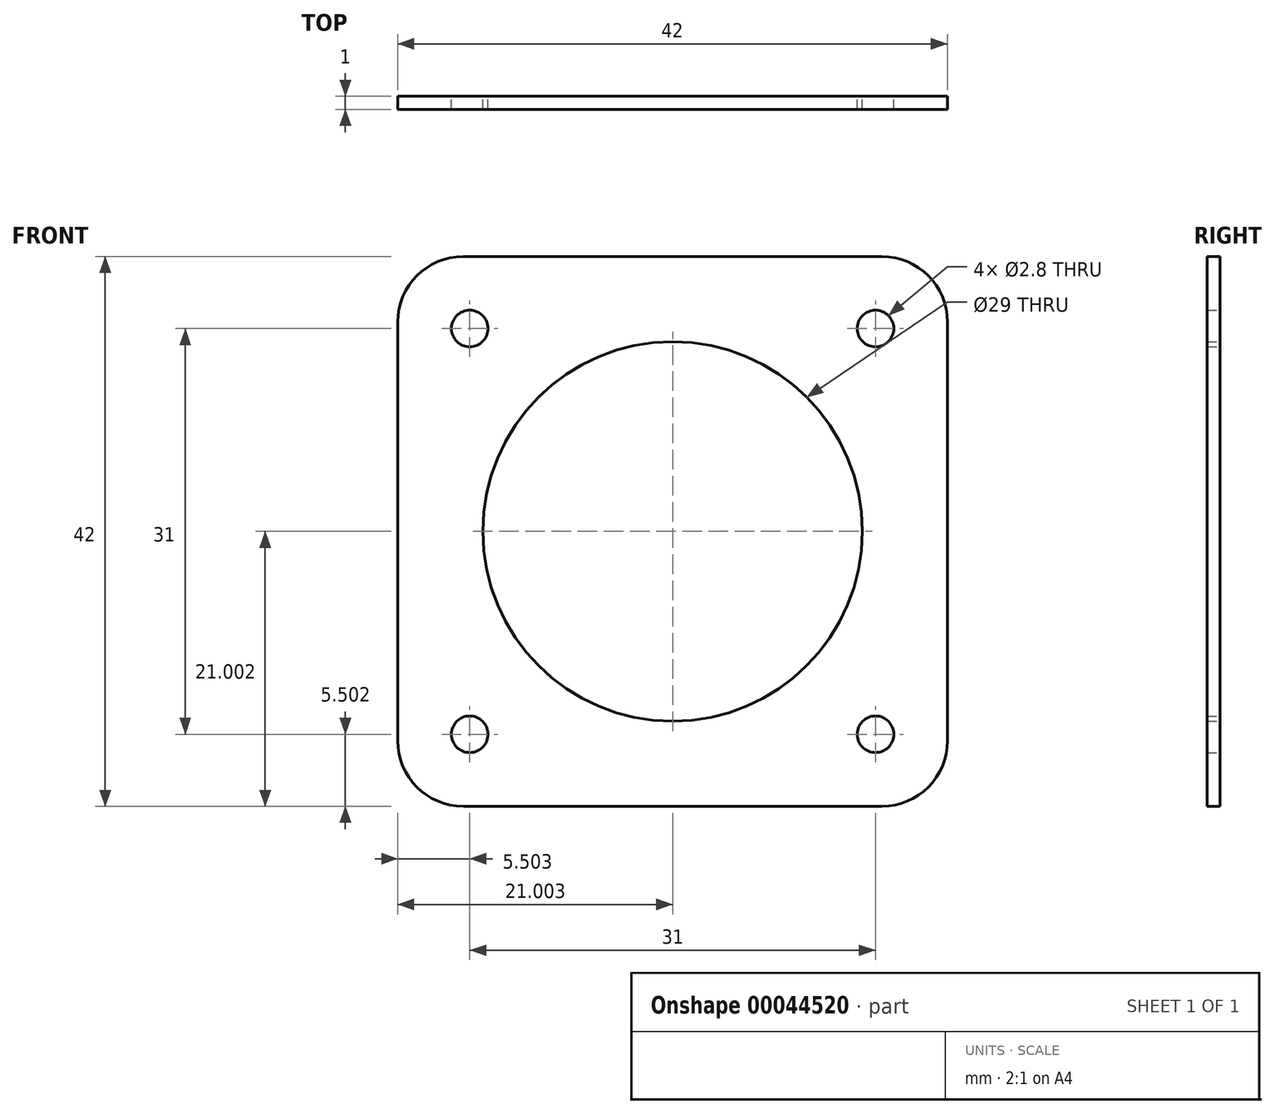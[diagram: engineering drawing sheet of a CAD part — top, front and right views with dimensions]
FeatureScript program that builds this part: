
annotation { "Feature Type Name" : "Feature", "Feature Type Description" : "" }
export const myFeature = defineFeature(function(context is Context, id is Id, definition is map)
    precondition{}
    {
        {
            var Q0;
            Q0=qCreatedBy(makeId("Front.planeOp"),FACE);
            var sketch = newSketch(context, id + "F0", { "sketchPlane" : qUnion([Q0])});
            skPoint(sketch, "E0", {"position": v(2.9, 11.96) * mm});
            skPoint(sketch, "E1", {"position": v(-28.1, 11.96) * mm});
            skPoint(sketch, "E2", {"position": v(-28.1, -19.04) * mm});
            skPoint(sketch, "E3", {"position": v(2.9, -19.04) * mm});
            skLineSegment(sketch, "E4.bottom", {"start": v(-33.6, 17.46) * mm, "end": v(8.4, 17.46) * mm});
            skLineSegment(sketch, "E4.top", {"start": v(-33.6, -24.54) * mm, "end": v(8.4, -24.54) * mm});
            skLineSegment(sketch, "E4.left", {"start": v(-33.6, 17.46) * mm, "end": v(-33.6, -24.54) * mm});
            skLineSegment(sketch, "E4.right", {"start": v(8.4, 17.46) * mm, "end": v(8.4, -24.54) * mm});
            skPoint(sketch, "E5", {"position": v(-12.6, -3.54) * mm});
            skSolve(sketch);
        }
        {
            var Q0;
            Q0=makeQuery(id+"F0.imprint","IMPRINT",FACE,{"disambiguationData":[TD([[makeQuery(id+"F0.imprint","IMPRINT",EDGE,{"derivedFrom":sQuery(id+"F0.wireOp",EDGE,"E4.bottom")}),-1.0]])]});
            extrude(context, id + "F1", {"entities" : qUnion([Q0]), "depth" : 1 * mm});
        }
        {
            var Q0;
            Q0=sQuery(id+"F0.wireOp",VERTEX,"E5");
            var Q1;
            Q1=makeQuery(id+"F1.opExtrude","SWEPT_BODY",BODY,{"disambiguationData":[OSD([sQuery(id+"F0.wireOp",EDGE,"E4.bottom"),sQuery(id+"F0.wireOp",EDGE,"E4.top"),sQuery(id+"F0.wireOp",EDGE,"E4.left"),sQuery(id+"F0.wireOp",EDGE,"E4.right")])]});
            hole(context, id + "F2", {"style" : HoleStyle.SIMPLE, "holeDiameter" : 29 * mm, "endStyle" : HoleEndStyle.THROUGH, "oppositeDirection" : true, "locations" : qUnion([Q0]), "scope" : qUnion([Q1])});
        }
        {
            var Q0;
            Q0=sQuery(id+"F0.wireOp",VERTEX,"E1");
            var Q1;
            Q1=sQuery(id+"F0.wireOp",VERTEX,"E0");
            var Q2;
            Q2=sQuery(id+"F0.wireOp",VERTEX,"E3");
            var Q3;
            Q3=sQuery(id+"F0.wireOp",VERTEX,"E2");
            var Q4;
            Q4=makeQuery(id+"F1.opExtrude","SWEPT_BODY",BODY,{"disambiguationData":[OSD([sQuery(id+"F0.wireOp",EDGE,"E4.bottom"),sQuery(id+"F0.wireOp",EDGE,"E4.top"),sQuery(id+"F0.wireOp",EDGE,"E4.left"),sQuery(id+"F0.wireOp",EDGE,"E4.right")])]});
            hole(context, id + "F3", {"style" : HoleStyle.SIMPLE, "holeDiameter" : 2.8 * mm, "endStyle" : HoleEndStyle.THROUGH, "oppositeDirection" : true, "locations" : qUnion([Q0, Q1, Q2, Q3]), "scope" : qUnion([Q4])});
        }
        {
            var Q0;
            Q0=makeQuery(id+"F1.opExtrude","SWEPT_EDGE",EDGE,{"disambiguationData":[OSD([sQuery(id+"F0.wireOp",EDGE,"E4.bottom"),sQuery(id+"F0.wireOp",EDGE,"E4.left")])]});
            var Q1;
            Q1=makeQuery(id+"F1.opExtrude","SWEPT_EDGE",EDGE,{"disambiguationData":[OSD([sQuery(id+"F0.wireOp",EDGE,"E4.top"),sQuery(id+"F0.wireOp",EDGE,"E4.left")])]});
            var Q2;
            Q2=makeQuery(id+"F1.opExtrude","SWEPT_EDGE",EDGE,{"disambiguationData":[OSD([sQuery(id+"F0.wireOp",EDGE,"E4.bottom"),sQuery(id+"F0.wireOp",EDGE,"E4.right")])]});
            var Q3;
            Q3=makeQuery(id+"F1.opExtrude","SWEPT_EDGE",EDGE,{"disambiguationData":[OSD([sQuery(id+"F0.wireOp",EDGE,"E4.top"),sQuery(id+"F0.wireOp",EDGE,"E4.right")])]});
            fillet(context, id + "F4", {"entities" : qUnion([Q0, Q1, Q2, Q3]), "radius" : 5 * mm, "tangentPropagation" : true, "allowEdgeOverflow" : false});
        }
    });
